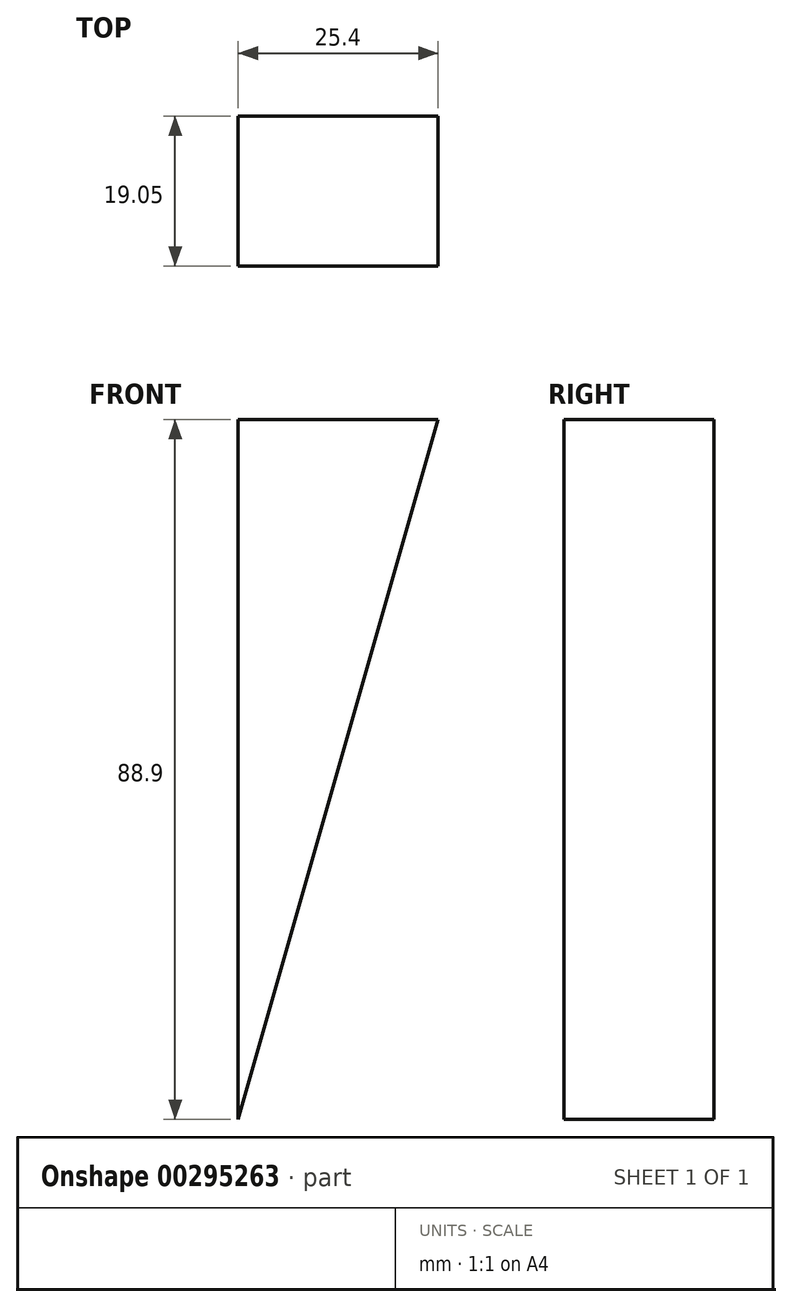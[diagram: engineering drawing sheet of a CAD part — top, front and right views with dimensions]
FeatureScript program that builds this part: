
annotation { "Feature Type Name" : "Feature", "Feature Type Description" : "" }
export const myFeature = defineFeature(function(context is Context, id is Id, definition is map)
    precondition{}
    {
        {
            var Q0;
            Q0=qCreatedBy(makeId("Front.planeOp"),FACE);
            var sketch = newSketch(context, id + "F0", { "sketchPlane" : qUnion([Q0])});
            skLineSegment(sketch, "E0", {"start": v(0, 0) * mm, "end": v(0, 88.9) * mm});
            skLineSegment(sketch, "E1", {"start": v(0, 88.9) * mm, "end": v(25.4, 88.9) * mm});
            skLineSegment(sketch, "E2", {"start": v(25.4, 88.9) * mm, "end": v(0, 0) * mm});
            skSolve(sketch);
        }
        {
            var Q0;
            Q0=makeQuery(id+"F0.imprint","IMPRINT",FACE,{"disambiguationData":[TD([[makeQuery(id+"F0.imprint","IMPRINT",EDGE,{"derivedFrom":sQuery(id+"F0.wireOp",EDGE,"E0")}),-1.0]])]});
            extrude(context, id + "F1", {"entities" : qUnion([Q0]), "depth" : 19.05 * mm});
        }
    });
